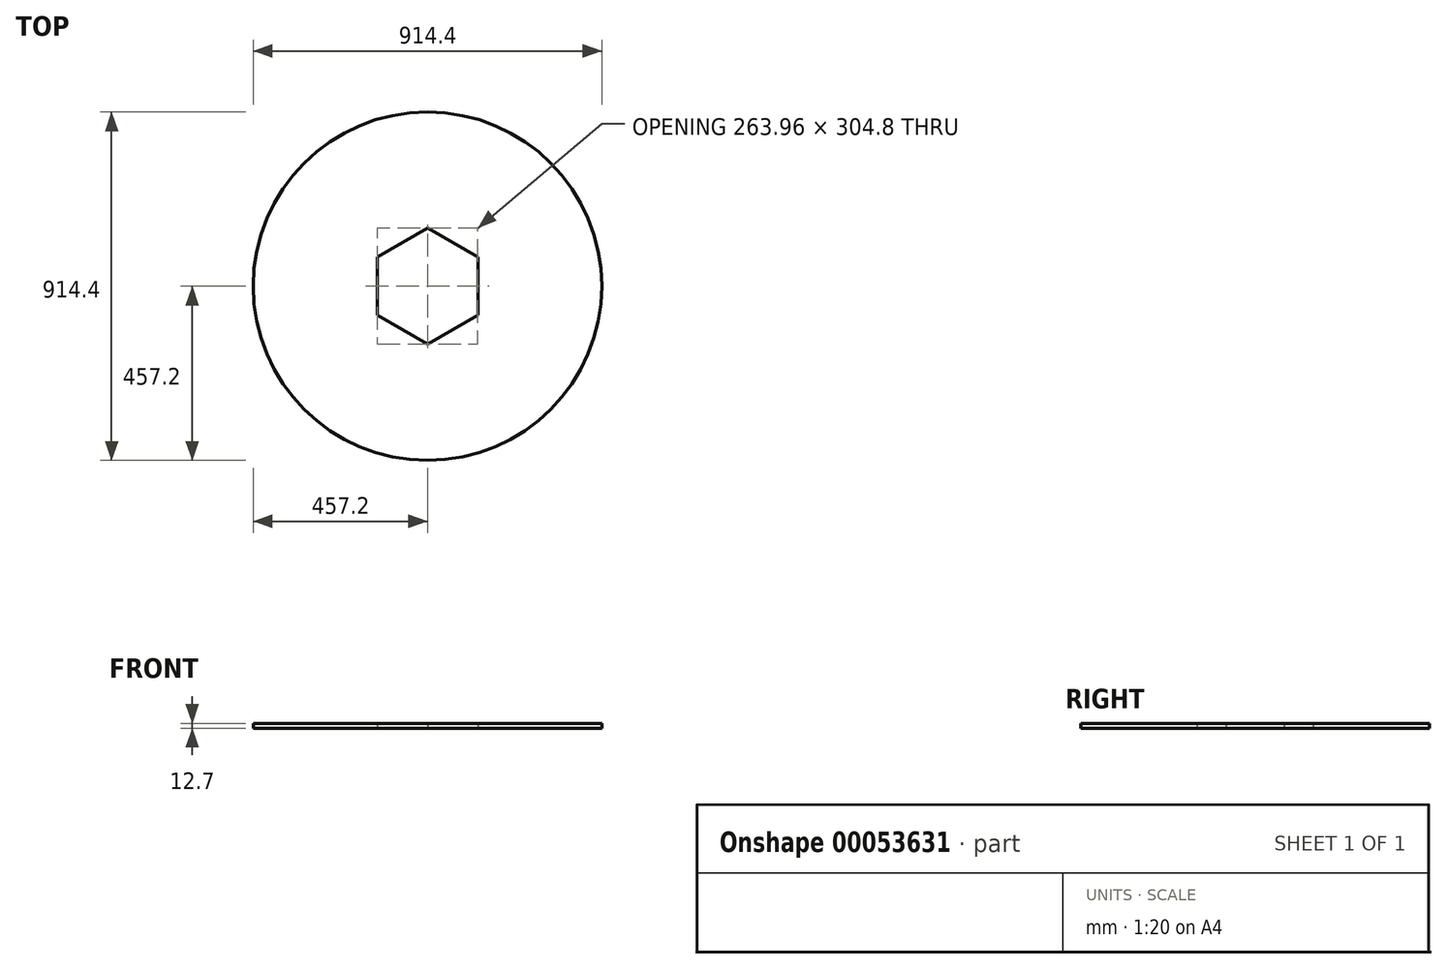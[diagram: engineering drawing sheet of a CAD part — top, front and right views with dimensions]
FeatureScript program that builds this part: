
annotation { "Feature Type Name" : "Feature", "Feature Type Description" : "" }
export const myFeature = defineFeature(function(context is Context, id is Id, definition is map)
    precondition{}
    {
        {
            var Q0;
            Q0=qCreatedBy(makeId("Top.planeOp"),FACE);
            var sketch = newSketch(context, id + "F0", { "sketchPlane" : qUnion([Q0])});
            skCircle(sketch, "E0", {"center": v(0, 0) * mm, "radius": 457.2 * mm});
            skCircle(sketch, "E1.cCircle", {"center": v(0, 0) * mm, "radius": 152.4 * mm, "construction": true});
            skLineSegment(sketch, "E1.0", {"start": v(0, 152.4) * mm, "end": v(131.98, 76.2) * mm});
            skLineSegment(sketch, "E1.1", {"start": v(131.98, 76.2) * mm, "end": v(131.98, -76.2) * mm});
            skLineSegment(sketch, "E1.2", {"start": v(131.98, -76.2) * mm, "end": v(0, -152.4) * mm});
            skLineSegment(sketch, "E1.3", {"start": v(0, -152.4) * mm, "end": v(-131.98, -76.2) * mm});
            skLineSegment(sketch, "E1.4", {"start": v(-131.98, -76.2) * mm, "end": v(-131.98, 76.2) * mm});
            skLineSegment(sketch, "E1.5", {"start": v(-131.98, 76.2) * mm, "end": v(0, 152.4) * mm});
            skSolve(sketch);
        }
        {
            var Q0;
            Q0=makeQuery(id+"F0.imprint","IMPRINT",FACE,{"disambiguationData":[TD([[makeQuery(id+"F0.imprint","IMPRINT",EDGE,{"derivedFrom":sQuery(id+"F0.wireOp",EDGE,"E0")}),1.0]])]});
            extrude(context, id + "F1", {"entities" : qUnion([Q0]), "depth" : 12.7 * mm});
        }
    });
